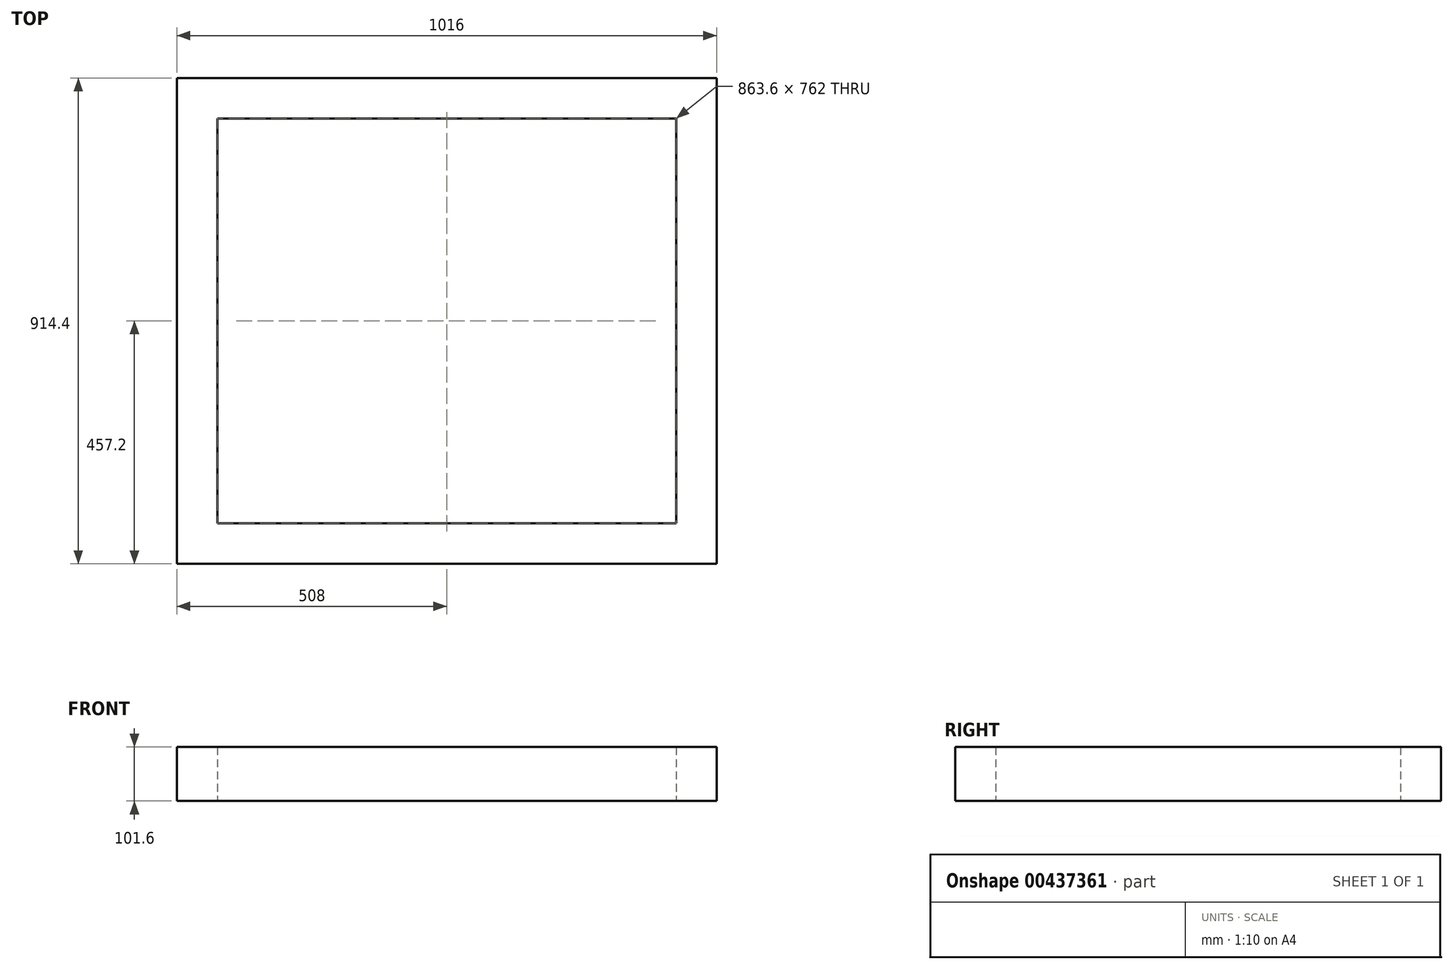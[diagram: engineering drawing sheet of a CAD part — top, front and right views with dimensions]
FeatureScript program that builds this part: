
annotation { "Feature Type Name" : "Feature", "Feature Type Description" : "" }
export const myFeature = defineFeature(function(context is Context, id is Id, definition is map)
    precondition{}
    {
        {
            var Q0;
            Q0=qCreatedBy(makeId("Top.planeOp"),FACE);
            var sketch = newSketch(context, id + "F0", { "sketchPlane" : qUnion([Q0])});
            skLineSegment(sketch, "E0.bottom", {"start": v(508, 457.2) * mm, "end": v(-508, 457.2) * mm});
            skLineSegment(sketch, "E0.top", {"start": v(508, -457.2) * mm, "end": v(-508, -457.2) * mm});
            skLineSegment(sketch, "E0.left", {"start": v(508, 457.2) * mm, "end": v(508, -457.2) * mm});
            skLineSegment(sketch, "E0.right", {"start": v(-508, 457.2) * mm, "end": v(-508, -457.2) * mm});
            skPoint(sketch, "E0.middle", {"position": v(0, 0) * mm});
            skLineSegment(sketch, "E1.bottom", {"start": v(431.8, 381) * mm, "end": v(-431.8, 381) * mm});
            skLineSegment(sketch, "E1.top", {"start": v(431.8, -381) * mm, "end": v(-431.8, -381) * mm});
            skLineSegment(sketch, "E1.left", {"start": v(431.8, 381) * mm, "end": v(431.8, -381) * mm});
            skLineSegment(sketch, "E1.right", {"start": v(-431.8, 381) * mm, "end": v(-431.8, -381) * mm});
            skSolve(sketch);
        }
        {
            var Q0;
            Q0 = qSketchRegion(id + "F0", true);
            extrude(context, id + "F1", {"entities" : qUnion([Q0]), "depth" : 101.6 * mm});
        }
    });
